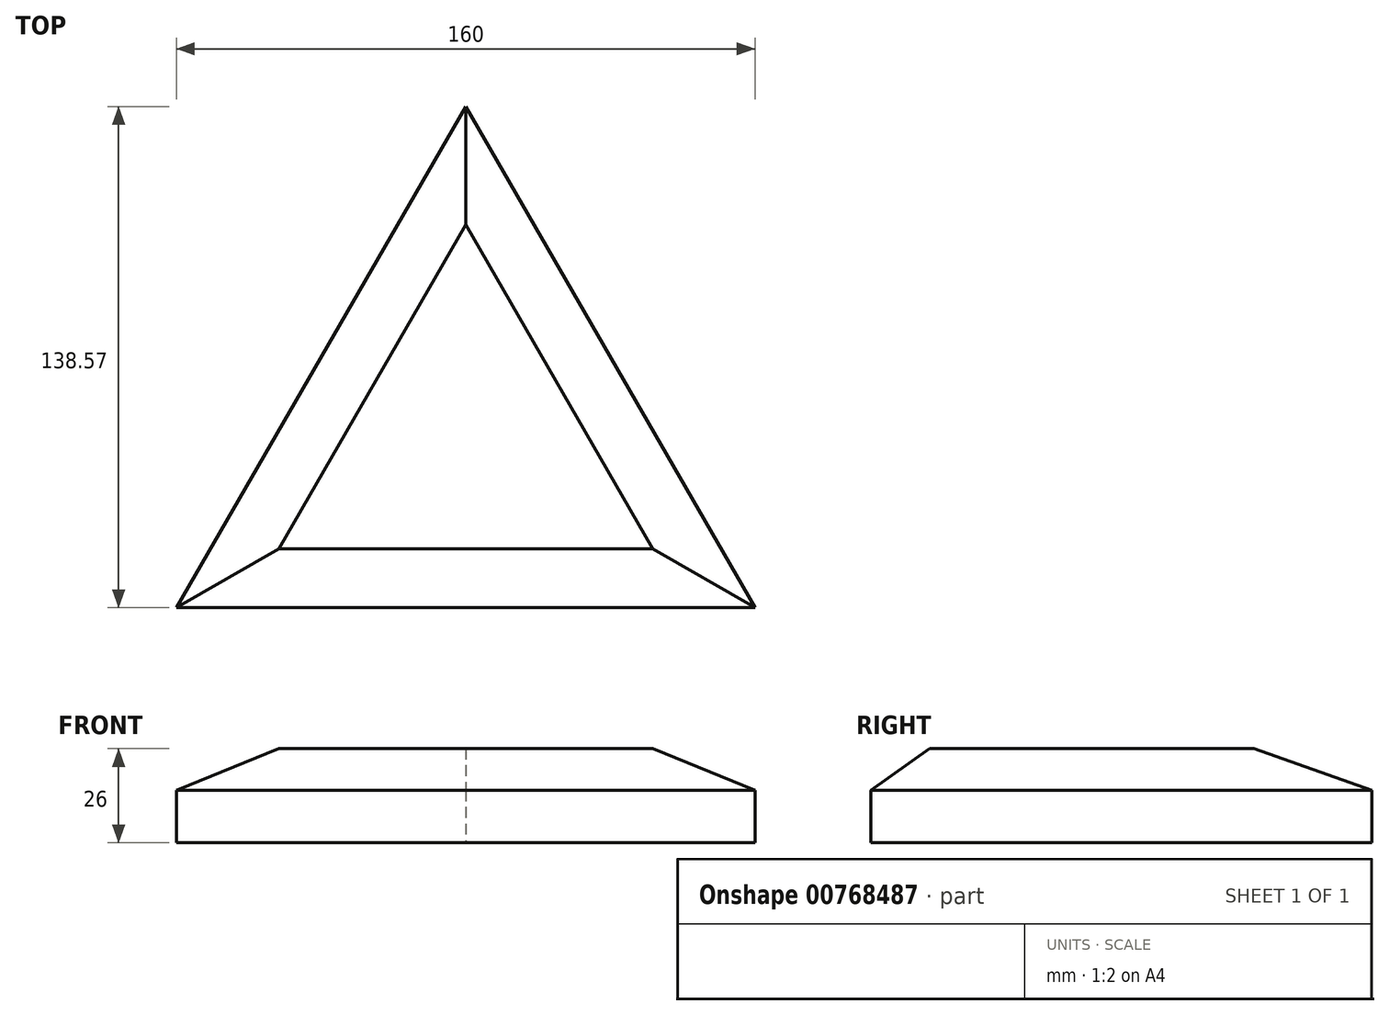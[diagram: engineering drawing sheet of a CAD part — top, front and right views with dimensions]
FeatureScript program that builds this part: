
annotation { "Feature Type Name" : "Feature", "Feature Type Description" : "" }
export const myFeature = defineFeature(function(context is Context, id is Id, definition is map)
    precondition{}
    {
        {
            var Q0;
            Q0=qCreatedBy(makeId("Top.planeOp"),FACE);
            var sketch = newSketch(context, id + "F0", { "sketchPlane" : qUnion([Q0])});
            skLineSegment(sketch, "E0.0", {"start": v(-80, -46.19) * mm, "end": v(0, 92.38) * mm});
            skLineSegment(sketch, "E0.1", {"start": v(0, 92.38) * mm, "end": v(80, -46.19) * mm});
            skLineSegment(sketch, "E0.2", {"start": v(80, -46.19) * mm, "end": v(-80, -46.19) * mm});
            skPoint(sketch, "E0.0.midPoint", {"position": v(-40, 23.1) * mm});
            skSolve(sketch);
        }
        {
            var Q0;
            Q0=makeQuery(id+"F0.imprint","IMPRINT",FACE,{"disambiguationData":[TD([[makeQuery(id+"F0.imprint","IMPRINT",EDGE,{"derivedFrom":sQuery(id+"F0.wireOp",EDGE,"E0.0")}),-1.0]])]});
            extrude(context, id + "F1", {"entities" : qUnion([Q0]), "depth" : 26 * mm, "offsetDistance" : 25 * mm});
        }
        {
            var Q0;
            Q0=makeQuery(id+"F1.opExtrude","CAP_EDGE",EDGE,{"disambiguationData":[OSD([sQuery(id+"F0.wireOp",EDGE,"E0.0")])],"isStart":false});
            var Q1;
            Q1=makeQuery(id+"F1.opExtrude","CAP_EDGE",EDGE,{"disambiguationData":[OSD([sQuery(id+"F0.wireOp",EDGE,"E0.1")])],"isStart":false});
            var Q2;
            Q2=makeQuery(id+"F1.opExtrude","CAP_EDGE",EDGE,{"disambiguationData":[OSD([sQuery(id+"F0.wireOp",EDGE,"E0.2")])],"isStart":false});
            chamfer(context, id + "F2", {"entities" : qUnion([Q0, Q1, Q2]), "chamferType" : ChamferType.OFFSET_ANGLE, "width" : 11.55 * mm, "oppositeDirection" : false, "angle" : 54.74 * degree, "tangentPropagation" : true});
        }
    });
